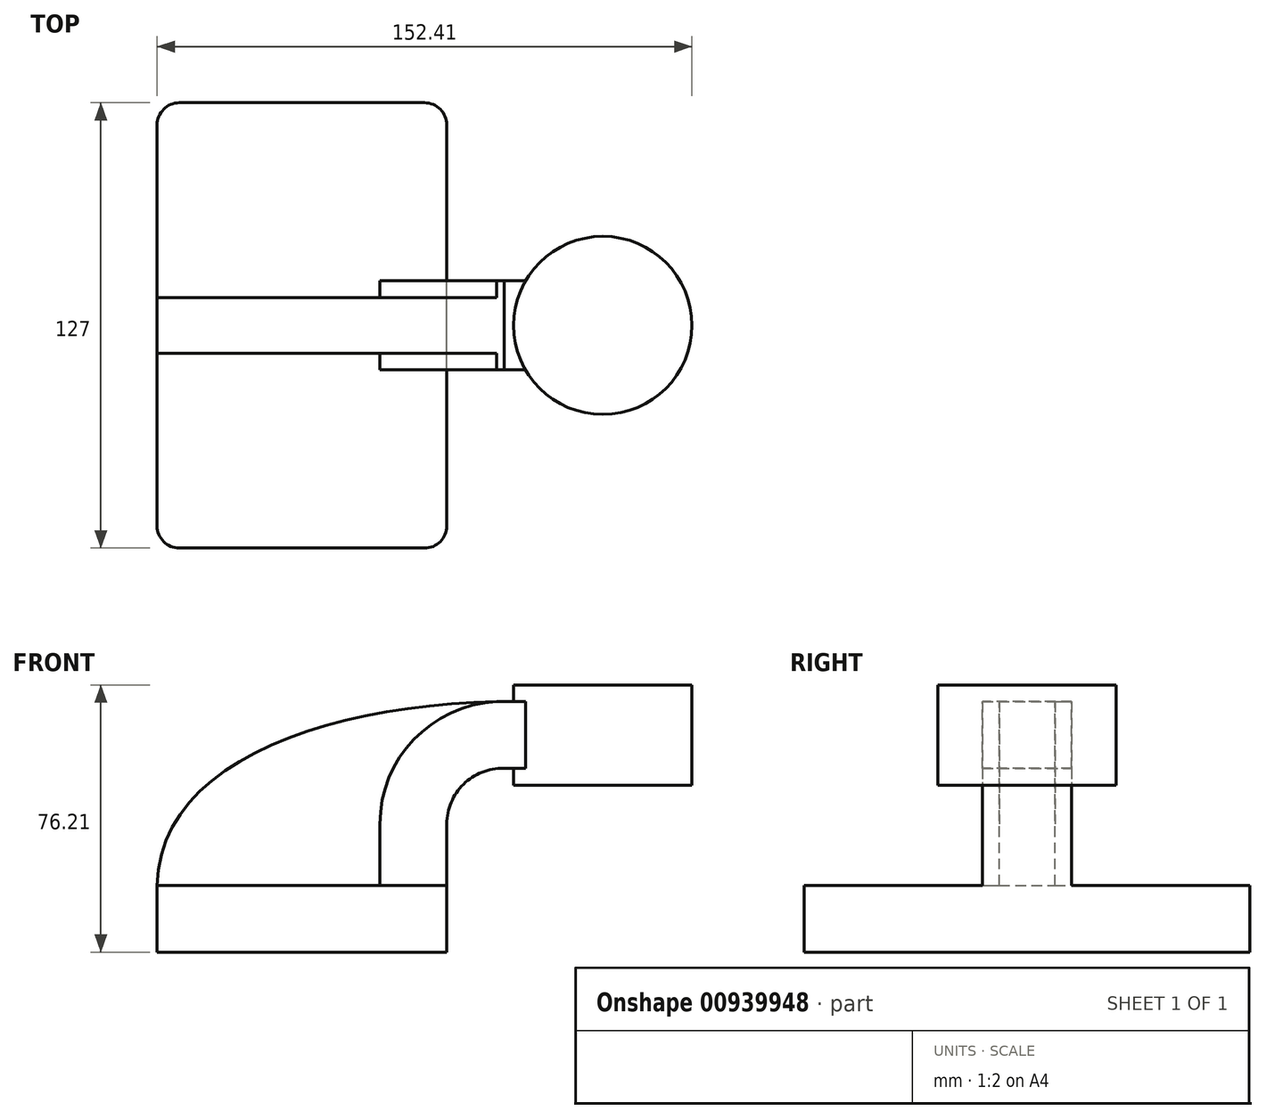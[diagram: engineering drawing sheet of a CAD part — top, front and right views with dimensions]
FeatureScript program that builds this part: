
annotation { "Feature Type Name" : "Feature", "Feature Type Description" : "" }
export const myFeature = defineFeature(function(context is Context, id is Id, definition is map)
    precondition{}
    {
        {
            var Q0;
            Q0=qCreatedBy(makeId("Front.planeOp"),FACE);
            var sketch = newSketch(context, id + "F0", { "sketchPlane" : qUnion([Q0])});
            skLineSegment(sketch, "E0.bottom", {"start": v(-41.28, 9.52) * mm, "end": v(41.27, 9.53) * mm});
            skLineSegment(sketch, "E0.top", {"start": v(-41.28, -9.52) * mm, "end": v(41.28, -9.52) * mm});
            skLineSegment(sketch, "E0.left", {"start": v(-41.28, 9.52) * mm, "end": v(-41.28, -9.52) * mm});
            skLineSegment(sketch, "E0.right", {"start": v(41.27, 9.53) * mm, "end": v(41.28, -9.52) * mm});
            skPoint(sketch, "E0.middle", {"position": v(0, 0) * mm});
            skLineSegment(sketch, "E1.bottom", {"start": v(111.12, 66.68) * mm, "end": v(60.32, 66.68) * mm});
            skLineSegment(sketch, "E1.top", {"start": v(111.13, 38.1) * mm, "end": v(60.32, 38.1) * mm});
            skLineSegment(sketch, "E1.left", {"start": v(111.12, 66.68) * mm, "end": v(111.12, 38.1) * mm});
            skLineSegment(sketch, "E1.right", {"start": v(60.32, 66.68) * mm, "end": v(60.32, 38.1) * mm});
            skLineSegment(sketch, "E2", {"start": v(41.27, 9.53) * mm, "end": v(41.27, 27) * mm});
            skArc(sketch, "E3", {"start": v(41.27, 27) * mm, "mid": v(46.04, 38.34) * mm, "end": v(57.47, 42.88) * mm});
            skLineSegment(sketch, "E4", {"start": v(57.47, 42.88) * mm, "end": v(85.72, 42.88) * mm});
            skLineSegment(sketch, "E5", {"start": v(85.72, 42.88) * mm, "end": v(85.72, 42.88) * mm});
            skPoint(sketch, "E5.endSnap0", {"position": v(85.72, 38.1) * mm});
            skLineSegment(sketch, "E6.0", {"start": v(57.62, 61.93) * mm, "end": v(85.72, 61.93) * mm});
            skArc(sketch, "E6.1", {"start": v(22.22, 27) * mm, "mid": v(32.62, 51.87) * mm, "end": v(57.62, 61.93) * mm});
            skLineSegment(sketch, "E6.2", {"start": v(22.22, 9.53) * mm, "end": v(22.22, 27) * mm});
            skLineSegment(sketch, "E7", {"start": v(85.72, 66.68) * mm, "end": v(85.72, 38.1) * mm});
            skFitSpline(sketch, "E8", {"points": [v(-41.28, 9.52) * mm, v(57.62, 61.93) * mm], "startDerivative": vector(2.1, 106.3) * mm, "endDerivative": vector(150.27, 1.99) * mm});
            skSolve(sketch);
        }
        {
            var Q0;
            Q0=makeQuery(id+"F0.imprint","IMPRINT",FACE,{"disambiguationData":[TD([[makeQuery(id+"F0.imprint","IMPRINT",EDGE,{"derivedFrom":sQuery(id+"F0.wireOp",EDGE,"E0.top")}),1.0]])]});
            extrude(context, id + "F1", {"entities" : qUnion([Q0]), "depth" : 127 * mm, "offsetDistance" : 25.4 * mm, "symmetric" : true});
        }
        {
            var Q0;
            {var subQ1=sQuery(id+"F0.wireOp",EDGE,"E2");Q0=makeQuery(id+"F0.imprint","IMPRINT",FACE,{"disambiguationData":[TD([[makeQuery(id+"F0.imprint","IMPRINT",EDGE,{"derivedFrom":subQ1}),1.0]])]});}
            var Q1;
            {var subQ0=sQuery(id+"F0.wireOp",EDGE,"E6.0");var subQ1=sQuery(id+"F0.wireOp",EDGE,"E1.right");var subQ2=makeQuery(id+"F0.imprint","INTERSECT",VERTEX,{"derivedFrom":[subQ1,subQ0]});Q1=makeQuery(id+"F0.imprint","IMPRINT",FACE,{"disambiguationData":[TD([[makeQuery(id+"F0.imprint","IMPRINT",EDGE,{"disambiguationData":[TD([[subQ2,-1.0]])],"derivedFrom":subQ1}),1.0]])]});}
            extrude(context, id + "F2", {"entities" : qUnion([Q0, Q1]), "operationType" : NewBodyOperationType.ADD, "depth" : 25.4 * mm, "offsetDistance" : 25.4 * mm, "symmetric" : true});
        }
        {
            var Q0;
            {var subQ3=sQuery(id+"F0.wireOp",EDGE,"E6.2");Q0=makeQuery(id+"F0.imprint","IMPRINT",FACE,{"disambiguationData":[TD([[makeQuery(id+"F0.imprint","IMPRINT",EDGE,{"derivedFrom":subQ3}),1.0]])]});}
            extrude(context, id + "F3", {"entities" : qUnion([Q0]), "operationType" : NewBodyOperationType.ADD, "depth" : 15.88 * mm, "offsetDistance" : 25.4 * mm, "symmetric" : true});
        }
        {
            var Q0;
            {var subQ0=sQuery(id+"F0.wireOp",EDGE,"E1.left");Q0=makeQuery(id+"F0.imprint","IMPRINT",FACE,{"disambiguationData":[TD([[makeQuery(id+"F0.imprint","IMPRINT",EDGE,{"derivedFrom":subQ0}),-1.0]])]});}
            var Q1;
            Q1=sQuery(id+"F0.wireOp",EDGE,"E7");
            revolve(context, id + "F4", {"operationType" : NewBodyOperationType.ADD, "surfaceOperationType" : NewSurfaceOperationType.NEW, "entities" : qUnion([Q0]), "axis" : qUnion([Q1]), "revolveType" : RevolveType.FULL});
        }
        {
            var Q0;
            Q0=makeQuery(id+"F1.opExtrude","CAP_EDGE",EDGE,{"disambiguationData":[OSD([sQuery(id+"F0.wireOp",EDGE,"E0.left")])],"isStart":true});
            var Q1;
            Q1=makeQuery(id+"F1.opExtrude","CAP_EDGE",EDGE,{"disambiguationData":[OSD([sQuery(id+"F0.wireOp",EDGE,"E0.left")])],"isStart":false});
            var Q2;
            Q2=makeQuery(id+"F1.opExtrude","CAP_EDGE",EDGE,{"disambiguationData":[OSD([sQuery(id+"F0.wireOp",EDGE,"E0.right")])],"isStart":false});
            var Q3;
            Q3=makeQuery(id+"F1.opExtrude","CAP_EDGE",EDGE,{"disambiguationData":[OSD([sQuery(id+"F0.wireOp",EDGE,"E0.right")])],"isStart":true});
            fillet(context, id + "F5", {"entities" : qUnion([Q0, Q1, Q2, Q3]), "radius" : 6.35 * mm, "tangentPropagation" : true, "allowEdgeOverflow" : false});
        }
    });
